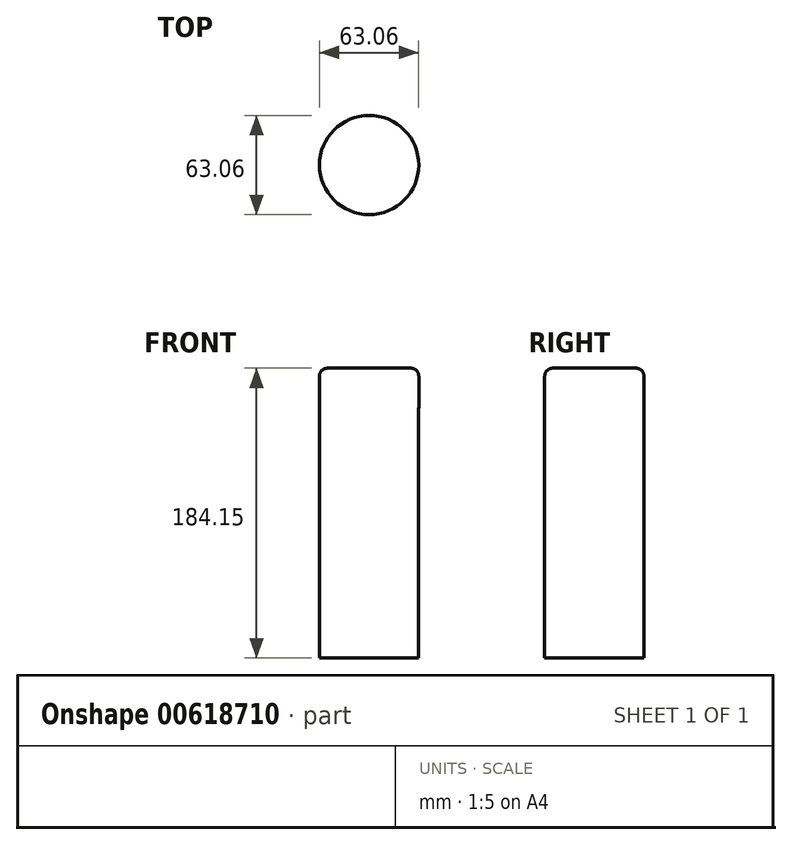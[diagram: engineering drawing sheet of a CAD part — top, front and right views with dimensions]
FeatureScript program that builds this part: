
annotation { "Feature Type Name" : "Feature", "Feature Type Description" : "" }
export const myFeature = defineFeature(function(context is Context, id is Id, definition is map)
    precondition{}
    {
        {
            var Q0;
            Q0=qCreatedBy(makeId("Top.planeOp"),FACE);
            var sketch = newSketch(context, id + "F0", { "sketchPlane" : qUnion([Q0])});
            skCircle(sketch, "E0", {"center": v(0, 0) * mm, "radius": 31.53 * mm});
            skSolve(sketch);
        }
        {
            var Q0;
            Q0=makeQuery(id+"F0.imprint","IMPRINT",FACE,{"disambiguationData":[TD([[makeQuery(id+"F0.imprint","IMPRINT",EDGE,{"derivedFrom":sQuery(id+"F0.wireOp",EDGE,"E0")}),1.0]])]});
            extrude(context, id + "F1", {"entities" : qUnion([Q0]), "depth" : 158.75 * mm, "offsetDistance" : 25.4 * mm});
        }
        {
            var Q0;
            Q0=makeQuery(id+"F1.opExtrude","CAP_FACE",FACE,{"disambiguationData":[OSD([sQuery(id+"F0.wireOp",EDGE,"E0")])],"isStart":false});
            var sketch = newSketch(context, id + "F2", { "sketchPlane" : qUnion([Q0])});
            skCircle(sketch, "E1", {"center": v(0, 0) * mm, "radius": 31.53 * mm});
            skSolve(sketch);
        }
        {
            var Q0;
            Q0 = qSketchRegion(id + "F2", true);
            extrude(context, id + "F3", {"entities" : qUnion([Q0]), "operationType" : NewBodyOperationType.ADD, "depth" : 25.4 * mm, "offsetDistance" : 25.4 * mm});
        }
        {
            var Q0;
            Q0=makeQuery(id+"F3.opExtrude","CAP_EDGE",EDGE,{"disambiguationData":[OSD([sQuery(id+"F2.wireOp",EDGE,"E1")])],"isStart":false});
            fillet(context, id + "F4", {"entities" : qUnion([Q0]), "radius" : 5.08 * mm, "tangentPropagation" : true, "allowEdgeOverflow" : false});
        }
    });
